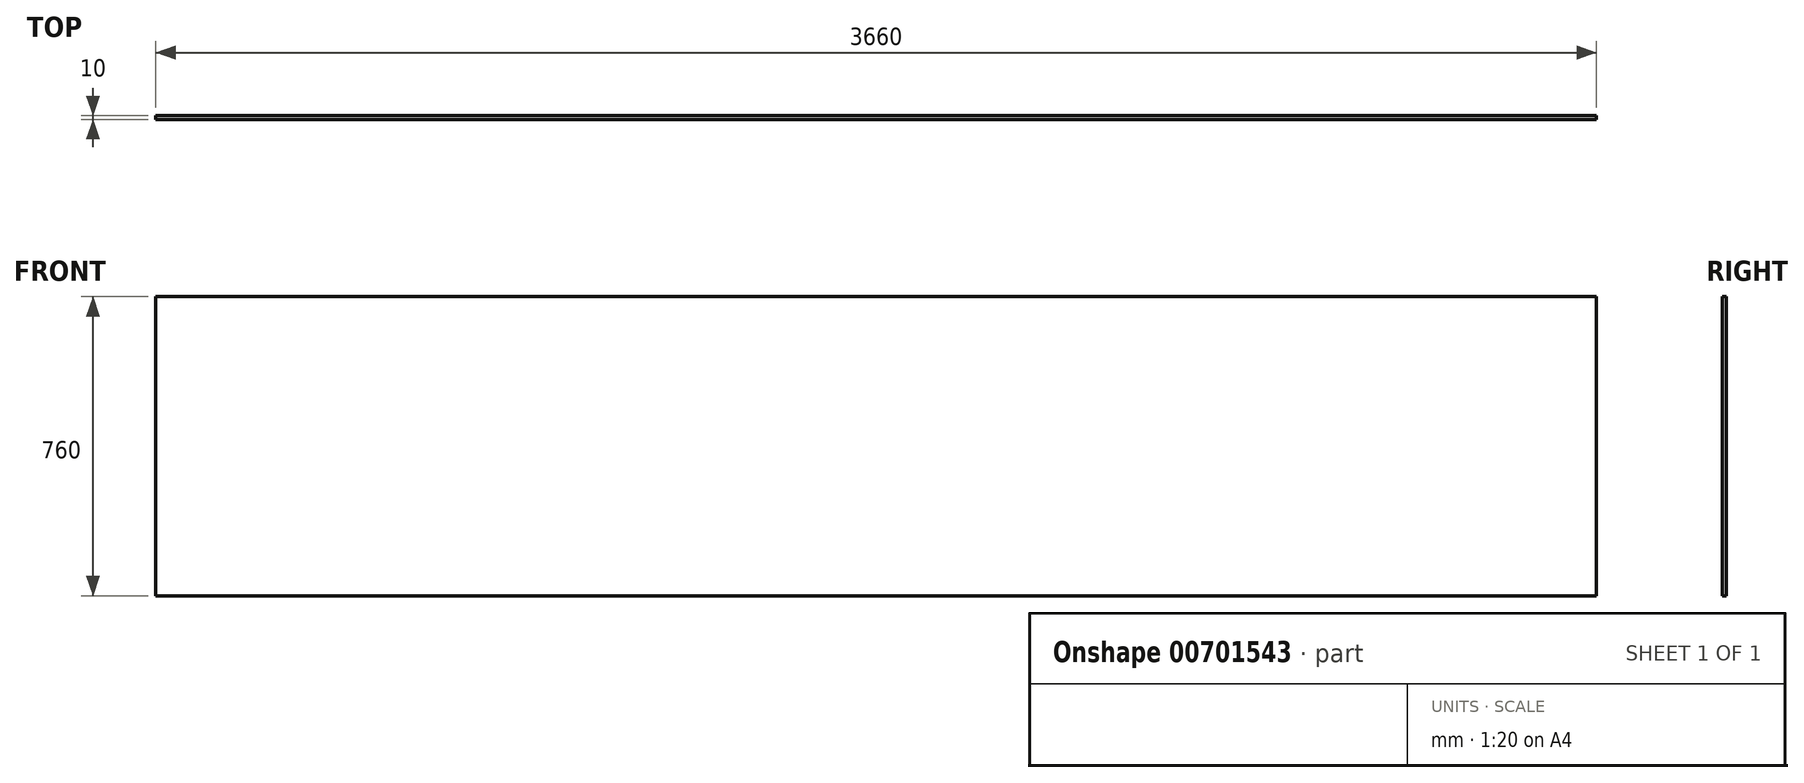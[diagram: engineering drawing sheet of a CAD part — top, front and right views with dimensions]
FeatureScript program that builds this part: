
annotation { "Feature Type Name" : "Feature", "Feature Type Description" : "" }
export const myFeature = defineFeature(function(context is Context, id is Id, definition is map)
    precondition{}
    {
        {
            var Q0;
            Q0=qCreatedBy(makeId("Front.planeOp"),FACE);
            var sketch = newSketch(context, id + "F0", { "sketchPlane" : qUnion([Q0])});
            skLineSegment(sketch, "E0.bottom", {"start": v(-1830, 380) * mm, "end": v(1830, 380) * mm});
            skLineSegment(sketch, "E0.top", {"start": v(-1830, -380) * mm, "end": v(1830, -380) * mm});
            skLineSegment(sketch, "E0.left", {"start": v(-1830, 380) * mm, "end": v(-1830, -380) * mm});
            skLineSegment(sketch, "E0.right", {"start": v(1830, 380) * mm, "end": v(1830, -380) * mm});
            skPoint(sketch, "E0.middle", {"position": v(0, 0) * mm});
            skSolve(sketch);
        }
        {
            var Q0;
            Q0=makeQuery(id+"F0.imprint","IMPRINT",FACE,{"disambiguationData":[TD([[makeQuery(id+"F0.imprint","IMPRINT",EDGE,{"derivedFrom":sQuery(id+"F0.wireOp",EDGE,"E0.bottom")}),-1.0]])]});
            extrude(context, id + "F1", {"entities" : qUnion([Q0]), "depth" : 10 * mm, "offsetDistance" : 25 * mm});
        }
    });
